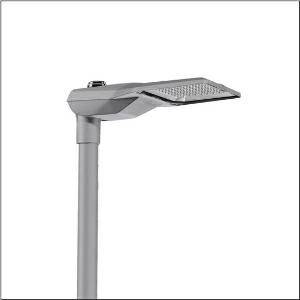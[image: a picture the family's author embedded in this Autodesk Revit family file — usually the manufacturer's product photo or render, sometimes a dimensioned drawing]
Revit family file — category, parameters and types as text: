
# Revit family: streetlight_sl_21_midi___pl52_5xe7h47n08lb_ccfd
name_source: partatom
category: Lighting Fixtures
units: mm (PartAtom-declared; Revit-internal decimal feet)

## family parameters
Cut with Voids When Loaded = No
Host = Face
Light Source = No
Part Type = Normal
Room Calculation Point = No
Round Connector Dimension = Use Diameter
Shared = No

## types (1)
- --- (1 x LED, 14690 lm, 98.3 W, 4000K)
    Apparent Load = 98 VA
    CIE Flux Codes = 27 59 98 100 100
    Color Rendering = 70
    Color Temperature = 4000K
    Default Elevation = 1800 mm
    Description = Streetlight SL 21 midi, mast luminaire, primary light control with lens, of PMMA, primary optical cover: cover, of toughened safety glass, transparent, light distribution: PL52, light emission: direct distribution, primary light characteristic: asymmetric, installation type: side-entry, LED, 3G 2.5mm², High Power LED, rated luminous flux: 14.690lm, luminous efficacy: 149lm/W, light colour: 740, colour temperature: 4000K, control gear: NEMA (7pin), control: overheat protection, pre-setting: linear dimming characteristic, constant luminous flux control, time-dependent luminous flux control, flexible luminous flux parameterisation, mains connection: 220..240V, AC, 50/60Hz, connection cable pre-assembled, cable length: 10,5m, wiring characteristics: H05VV-F, start of lifetime: 98W, end of service life: 101W, reduction: 45W, luminaire housing, of diecast aluminium (EN AC-44300), powder-coated, Siteco® metallic grey (DB 702S), corrosivity category C5 mid according to DIN EN ISO 12944, multi-level sealing system, sealing non-destructively replaceable, inclination adjustable: 0°, 5°, 10°, 15°, length: 644mm, width: 335mm, height: 110mm, spigot size: 42mm (side-entry), mounting height: 4..8m, protection rating (complete): IP66, insulation class (complete): insulation class I (protective earthing), certification: CE, ENEC, ENEC+, VDE, impact resistance: IK09, permissible operating ambient temperature for outdoor applications: -40..+50°C, standard-compliant lighting for roads and squares, packaging unit: 1 piece

Light Distribution: PL52
    Height = 111 mm
    Lamp = 1 x LED
    Lamp Light Flux = 14690 lm
    Lamp Power = 98.3 W
    Lamp count = 1
    Length = 644 mm
    Luminous efficacy = 149 lm/W
    Manufacturer = Siteco
    ModVariant = No
    Model = 5XE7H47N08LB
    Number of Poles = 1
    OnlyDefault = Yes
    Power Factor = 1
    Product Name = Streetlight SL 21 midi | PL52
    Product group = mast luminaire | pylon top
    ProductGroupID = 6100
    Protection Class = Protection class I
    Protection Degree = IP 66
    RLX_Detail_Level = 1
    RLX_Emergency_Light_Flux = 0 lm
    RLX_Emergency_Type = 0
    RLX_Emergency_Type_DB = No
    RlxData = <blob elided: 100533 chars, md5=835904da>
    Socket = socket
    Standby Power = 0 W
    System Light Flux = 14690 lm
    System Power = 98 W
    Type Comments = factory setting: luminous flux: 100 % | dim-lin: 254 | 1020 mA
    Type Image = l_1294377.jpg
    URL = http://relux.com
    VarID = @adj_132154
    Voltage = 0 V
    Weight = 0.00 kg
    Width = 336 mm

## geometry (parser evidence)
native form markers: Blend x4, Sweep x12
no freeform markers — native parametric forms only
